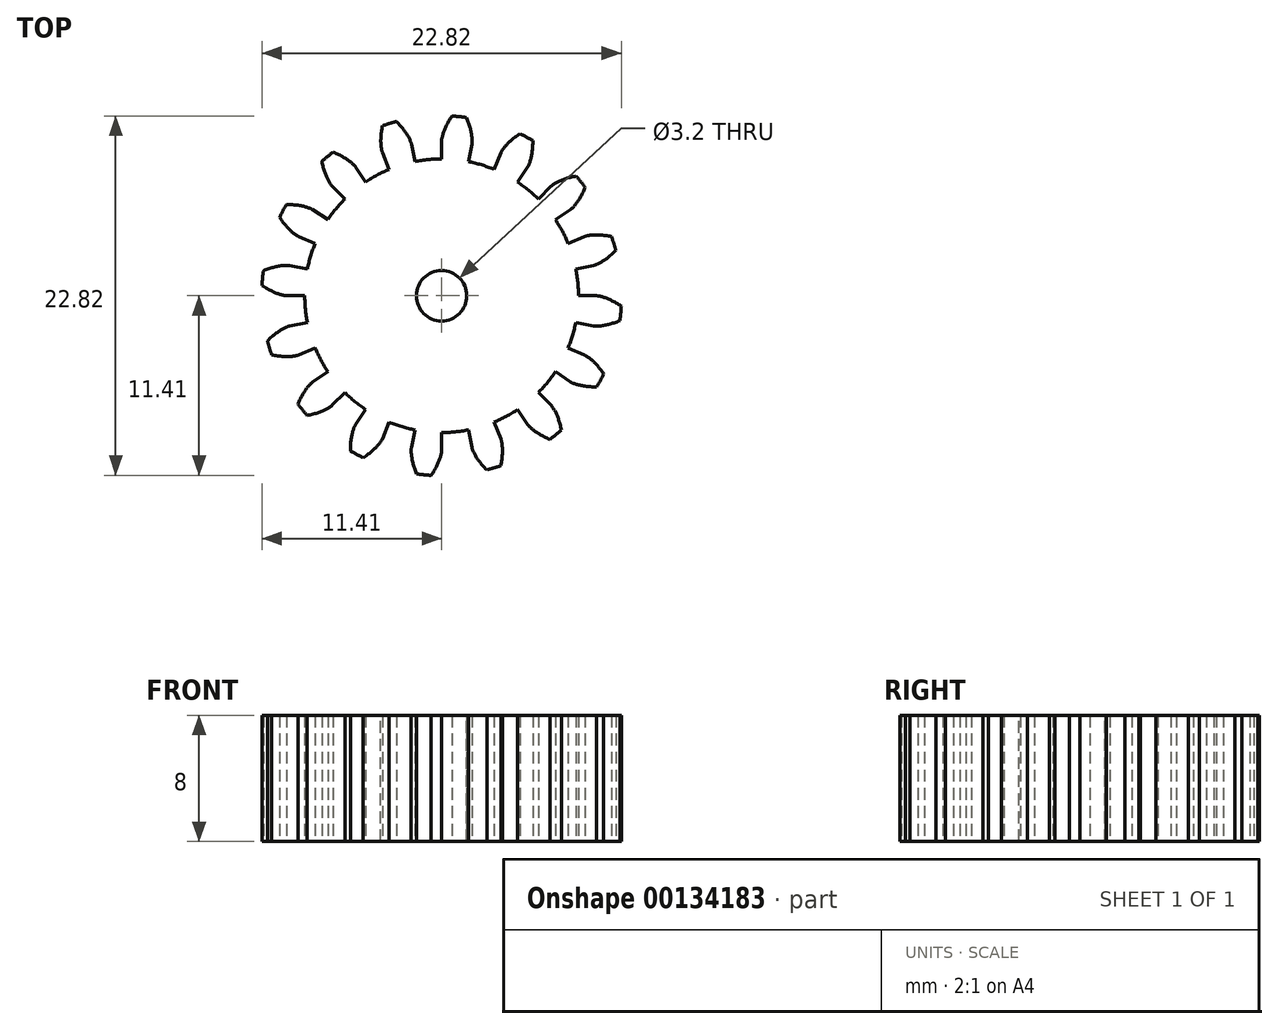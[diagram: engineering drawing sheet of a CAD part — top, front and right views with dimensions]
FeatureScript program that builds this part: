
annotation { "Feature Type Name" : "Feature", "Feature Type Description" : "" }
export const myFeature = defineFeature(function(context is Context, id is Id, definition is map)
    precondition{}
    {
        {
            assignVariable(context, id + "F0", {"name" : "NumberTeeth", "anyValue" : 16});
        }
        {
            assignVariable(context, id + "F1", {"name" : "GearThickness", "anyValue" : 8});
        }
        {
            var Q0;
            Q0=qCreatedBy(makeId("Top.planeOp"),FACE);
            var sketch = newSketch(context, id + "F2", { "sketchPlane" : qUnion([Q0])});
            skCircle(sketch, "E0", {"center": v(0, 0) * mm, "radius": 8.7 * mm});
            skCircle(sketch, "E1", {"center": v(0, 0) * mm, "radius": 9.84 * mm, "construction": true});
            skCircle(sketch, "E2", {"center": v(0, 0) * mm, "radius": 10.16 * mm, "construction": true});
            skCircle(sketch, "E3", {"center": v(0, 0) * mm, "radius": 11.43 * mm});
            skLineSegment(sketch, "E4", {"start": v(0, 0) * mm, "end": v(-9.84, 0) * mm, "construction": true});
            skLineSegment(sketch, "E5.1.0", {"start": v(0, 0) * mm, "end": v(-9.82, 0.5) * mm, "construction": true});
            skLineSegment(sketch, "E5.2.0", {"start": v(0, 0) * mm, "end": v(-9.79, 0.98) * mm, "construction": true});
            skLineSegment(sketch, "E5.3.0", {"start": v(0, 0) * mm, "end": v(-9.73, 1.47) * mm, "construction": true});
            skLineSegment(sketch, "E5.4.0", {"start": v(0, 0) * mm, "end": v(-9.64, 1.95) * mm, "construction": true});
            skLineSegment(sketch, "E5.5.0", {"start": v(0, 0) * mm, "end": v(-9.53, 2.43) * mm, "construction": true});
            skLineSegment(sketch, "E5.6.0", {"start": v(0, 0) * mm, "end": v(-9.4, 2.9) * mm, "construction": true});
            skLineSegment(sketch, "E5.7.0", {"start": v(0, 0) * mm, "end": v(-9.24, 3.37) * mm, "construction": true});
            skLineSegment(sketch, "E5.8.0", {"start": v(0, 0) * mm, "end": v(-9.06, 3.83) * mm, "construction": true});
            skLineSegment(sketch, "E5.9.0", {"start": v(0, 0) * mm, "end": v(-8.86, 4.28) * mm, "construction": true});
            skLineSegment(sketch, "E5.10.0", {"start": v(0, 0) * mm, "end": v(-8.63, 4.72) * mm, "construction": true});
            skLineSegment(sketch, "E5.11.0", {"start": v(0, 0) * mm, "end": v(-8.39, 5.14) * mm, "construction": true});
            skLineSegment(sketch, "E5.12.0", {"start": v(0, 0) * mm, "end": v(-8.12, 5.55) * mm, "construction": true});
            skLineSegment(sketch, "E5.13.0", {"start": v(0, 0) * mm, "end": v(-7.83, 5.95) * mm, "construction": true});
            skLineSegment(sketch, "E5.14.0", {"start": v(0, 0) * mm, "end": v(-7.52, 6.34) * mm, "construction": true});
            skLineSegment(sketch, "E5.anchor2", {"start": v(0, 0) * mm, "end": v(-7.52, 6.34) * mm, "construction": true});
            skLineSegment(sketch, "E6", {"start": v(-9.82, 0.5) * mm, "end": v(-9.85, 0) * mm, "construction": true});
            skLineSegment(sketch, "E7", {"start": v(-9.79, 0.98) * mm, "end": v(-9.89, 0) * mm, "construction": true});
            skLineSegment(sketch, "E8", {"start": v(-9.73, 1.47) * mm, "end": v(-9.95, 0.01) * mm, "construction": true});
            skLineSegment(sketch, "E9", {"start": v(-9.53, 2.43) * mm, "end": v(-10.14, 0.05) * mm, "construction": true});
            skLineSegment(sketch, "E10", {"start": v(-9.4, 2.9) * mm, "end": v(-10.27, 0.09) * mm, "construction": true});
            skLineSegment(sketch, "E11", {"start": v(-9.24, 3.37) * mm, "end": v(-10.42, 0.14) * mm, "construction": true});
            skLineSegment(sketch, "E12", {"start": v(-9.06, 3.83) * mm, "end": v(-10.6, 0.2) * mm, "construction": true});
            skLineSegment(sketch, "E13", {"start": v(-8.86, 4.28) * mm, "end": v(-10.78, 0.3) * mm, "construction": true});
            skLineSegment(sketch, "E14", {"start": v(-8.63, 4.72) * mm, "end": v(-11, 0.4) * mm, "construction": true});
            skLineSegment(sketch, "E15", {"start": v(-8.39, 5.14) * mm, "end": v(-11.21, 0.53) * mm, "construction": true});
            skLineSegment(sketch, "E16", {"start": v(-9.64, 1.95) * mm, "end": v(-10.03, 0.03) * mm, "construction": true});
            skLineSegment(sketch, "E17", {"start": v(-8.12, 5.55) * mm, "end": v(-11.45, 0.68) * mm, "construction": true});
            skLineSegment(sketch, "E18", {"start": v(-7.83, 5.95) * mm, "end": v(-11.7, 0.86) * mm, "construction": true});
            skLineSegment(sketch, "E19", {"start": v(-7.52, 6.34) * mm, "end": v(-11.96, 1.07) * mm, "construction": true});
            skLineSegment(sketch, "E20", {"start": v(0, 0) * mm, "end": v(-9.79, 0.96) * mm, "construction": true});
            skLineSegment(sketch, "E21", {"start": v(-8.7, 0) * mm, "end": v(-9.84, 0) * mm});
            skLineSegment(sketch, "E22.MirrorCS", {"start": v(-8.52, 1.7) * mm, "end": v(-9.65, 1.92) * mm});
            skFitSpline(sketch, "E23", {"points": [v(-9.84, 0) * mm, v(-9.85, 0) * mm, v(-9.89, 0) * mm, v(-9.95, 0.01) * mm, v(-10.03, 0.03) * mm, v(-10.14, 0.05) * mm, v(-10.27, 0.09) * mm, v(-10.42, 0.14) * mm, v(-10.6, 0.2) * mm, v(-10.78, 0.3) * mm, v(-11, 0.4) * mm, v(-11.21, 0.53) * mm, v(-11.45, 0.68) * mm, v(-11.7, 0.86) * mm, v(-11.96, 1.07) * mm], "startDerivative": vector(-0.85, 0) * mm, "endDerivative": vector(-1.05, 0.88) * mm});
            skLineSegment(sketch, "E24", {"start": v(-11.96, 1.07) * mm, "end": v(-16.54, 4.93) * mm, "construction": true});
            skFitSpline(sketch, "E25.MirrorCS", {"points": [v(-9.65, 1.92) * mm, v(-9.66, 1.92) * mm, v(-9.7, 1.93) * mm, v(-9.76, 1.93) * mm, v(-9.84, 1.93) * mm, v(-9.95, 1.93) * mm, v(-10.09, 1.92) * mm, v(-10.25, 1.9) * mm, v(-10.43, 1.86) * mm, v(-10.63, 1.82) * mm, v(-10.86, 1.75) * mm, v(-11.1, 1.67) * mm, v(-11.36, 1.56) * mm, v(-11.64, 1.44) * mm, v(-11.94, 1.28) * mm], "startDerivative": vector(-0.84, 0.17) * mm, "endDerivative": vector(-1.2, -0.66) * mm});
            skSolve(sketch);
        }
        {
            var Q0;
            {var subQ0=sQuery(id+"F2.wireOp",EDGE,"E0");var subQ27=makeQuery(id+"F2.imprint","INTERSECT",VERTEX,{"derivedFrom":[subQ0,sQuery(id+"F2.wireOp",EDGE,"10ea1024-8cf5-41f5-a75f-a634b86921f3.10.0")]});Q0=makeQuery(id+"F2.imprint","IMPRINT",FACE,{"disambiguationData":[TD([[makeQuery(id+"F2.imprint","IMPRINT",EDGE,{"disambiguationData":[TD([[subQ27,-1.0]])],"derivedFrom":subQ0}),1.0]])]});}
            var Q1;
            {var subQ0=sQuery(id+"F2.wireOp",EDGE,"10ea1024-8cf5-41f5-a75f-a634b86921f3.1.0");Q1=makeQuery(id+"F2.imprint","IMPRINT",FACE,{"disambiguationData":[TD([[makeQuery(id+"F2.imprint","IMPRINT",EDGE,{"derivedFrom":subQ0}),-1.0]])]});}
            var Q2;
            {var subQ7=sQuery(id+"F2.wireOp",EDGE,"10ea1024-8cf5-41f5-a75f-a634b86921f3.2.0");Q2=makeQuery(id+"F2.imprint","IMPRINT",FACE,{"disambiguationData":[TD([[makeQuery(id+"F2.imprint","IMPRINT",EDGE,{"derivedFrom":subQ7}),-1.0]])]});}
            var Q3;
            {var subQ8=sQuery(id+"F2.wireOp",EDGE,"10ea1024-8cf5-41f5-a75f-a634b86921f3.3.0");Q3=makeQuery(id+"F2.imprint","IMPRINT",FACE,{"disambiguationData":[TD([[makeQuery(id+"F2.imprint","IMPRINT",EDGE,{"derivedFrom":subQ8}),-1.0]])]});}
            var Q4;
            {var subQ2=sQuery(id+"F2.wireOp",EDGE,"10ea1024-8cf5-41f5-a75f-a634b86921f3.4.0");Q4=makeQuery(id+"F2.imprint","IMPRINT",FACE,{"disambiguationData":[TD([[makeQuery(id+"F2.imprint","IMPRINT",EDGE,{"derivedFrom":subQ2}),-1.0]])]});}
            var Q5;
            {var subQ8=sQuery(id+"F2.wireOp",EDGE,"10ea1024-8cf5-41f5-a75f-a634b86921f3.5.0");Q5=makeQuery(id+"F2.imprint","IMPRINT",FACE,{"disambiguationData":[TD([[makeQuery(id+"F2.imprint","IMPRINT",EDGE,{"derivedFrom":subQ8}),-1.0]])]});}
            var Q6;
            {var subQ3=sQuery(id+"F2.wireOp",EDGE,"10ea1024-8cf5-41f5-a75f-a634b86921f3.6.0");Q6=makeQuery(id+"F2.imprint","IMPRINT",FACE,{"disambiguationData":[TD([[makeQuery(id+"F2.imprint","IMPRINT",EDGE,{"derivedFrom":subQ3}),-1.0]])]});}
            var Q7;
            {var subQ0=sQuery(id+"F2.wireOp",EDGE,"10ea1024-8cf5-41f5-a75f-a634b86921f3.7.0");Q7=makeQuery(id+"F2.imprint","IMPRINT",FACE,{"disambiguationData":[TD([[makeQuery(id+"F2.imprint","IMPRINT",EDGE,{"derivedFrom":subQ0}),-1.0]])]});}
            var Q8;
            {var subQ5=sQuery(id+"F2.wireOp",EDGE,"10ea1024-8cf5-41f5-a75f-a634b86921f3.8.0");Q8=makeQuery(id+"F2.imprint","IMPRINT",FACE,{"disambiguationData":[TD([[makeQuery(id+"F2.imprint","IMPRINT",EDGE,{"derivedFrom":subQ5}),-1.0]])]});}
            var Q9;
            {var subQ1=sQuery(id+"F2.wireOp",EDGE,"10ea1024-8cf5-41f5-a75f-a634b86921f3.9.0");Q9=makeQuery(id+"F2.imprint","IMPRINT",FACE,{"disambiguationData":[TD([[makeQuery(id+"F2.imprint","IMPRINT",EDGE,{"derivedFrom":subQ1}),-1.0]])]});}
            var Q10;
            {var subQ5=sQuery(id+"F2.wireOp",EDGE,"10ea1024-8cf5-41f5-a75f-a634b86921f3.10.0");Q10=makeQuery(id+"F2.imprint","IMPRINT",FACE,{"disambiguationData":[TD([[makeQuery(id+"F2.imprint","IMPRINT",EDGE,{"derivedFrom":subQ5}),-1.0]])]});}
            var Q11;
            {var subQ8=sQuery(id+"F2.wireOp",EDGE,"10ea1024-8cf5-41f5-a75f-a634b86921f3.11.0");Q11=makeQuery(id+"F2.imprint","IMPRINT",FACE,{"disambiguationData":[TD([[makeQuery(id+"F2.imprint","IMPRINT",EDGE,{"derivedFrom":subQ8}),-1.0]])]});}
            var Q12;
            {var subQ2=sQuery(id+"F2.wireOp",EDGE,"10ea1024-8cf5-41f5-a75f-a634b86921f3.12.0");Q12=makeQuery(id+"F2.imprint","IMPRINT",FACE,{"disambiguationData":[TD([[makeQuery(id+"F2.imprint","IMPRINT",EDGE,{"derivedFrom":subQ2}),-1.0]])]});}
            var Q13;
            {var subQ3=sQuery(id+"F2.wireOp",EDGE,"10ea1024-8cf5-41f5-a75f-a634b86921f3.13.0");Q13=makeQuery(id+"F2.imprint","IMPRINT",FACE,{"disambiguationData":[TD([[makeQuery(id+"F2.imprint","IMPRINT",EDGE,{"derivedFrom":subQ3}),-1.0]])]});}
            var Q14;
            {var subQ0=sQuery(id+"F2.wireOp",EDGE,"10ea1024-8cf5-41f5-a75f-a634b86921f3.14.0");Q14=makeQuery(id+"F2.imprint","IMPRINT",FACE,{"disambiguationData":[TD([[makeQuery(id+"F2.imprint","IMPRINT",EDGE,{"derivedFrom":subQ0}),-1.0]])]});}
            var Q15;
            {var subQ6=sQuery(id+"F2.wireOp",EDGE,"10ea1024-8cf5-41f5-a75f-a634b86921f3.15.0");Q15=makeQuery(id+"F2.imprint","IMPRINT",FACE,{"disambiguationData":[TD([[makeQuery(id+"F2.imprint","IMPRINT",EDGE,{"derivedFrom":subQ6}),-1.0]])]});}
            var Q16;
            {var subQ5=sQuery(id+"F2.wireOp",EDGE,"10ea1024-8cf5-41f5-a75f-a634b86921f3.16.0");Q16=makeQuery(id+"F2.imprint","IMPRINT",FACE,{"disambiguationData":[TD([[makeQuery(id+"F2.imprint","IMPRINT",EDGE,{"derivedFrom":subQ5}),-1.0]])]});}
            var Q17;
            {var subQ7=sQuery(id+"F2.wireOp",EDGE,"10ea1024-8cf5-41f5-a75f-a634b86921f3.17.0");Q17=makeQuery(id+"F2.imprint","IMPRINT",FACE,{"disambiguationData":[TD([[makeQuery(id+"F2.imprint","IMPRINT",EDGE,{"derivedFrom":subQ7}),-1.0]])]});}
            var Q18;
            {var subQ5=sQuery(id+"F2.wireOp",EDGE,"10ea1024-8cf5-41f5-a75f-a634b86921f3.18.0");Q18=makeQuery(id+"F2.imprint","IMPRINT",FACE,{"disambiguationData":[TD([[makeQuery(id+"F2.imprint","IMPRINT",EDGE,{"derivedFrom":subQ5}),-1.0]])]});}
            var Q19;
            {var subQ8=sQuery(id+"F2.wireOp",EDGE,"10ea1024-8cf5-41f5-a75f-a634b86921f3.19.0");Q19=makeQuery(id+"F2.imprint","IMPRINT",FACE,{"disambiguationData":[TD([[makeQuery(id+"F2.imprint","IMPRINT",EDGE,{"derivedFrom":subQ8}),-1.0]])]});}
            var Q20;
            {var subQ8=sQuery(id+"F2.wireOp",EDGE,"E21");Q20=makeQuery(id+"F2.imprint","IMPRINT",FACE,{"disambiguationData":[TD([[makeQuery(id+"F2.imprint","IMPRINT",EDGE,{"derivedFrom":subQ8}),-1.0]])]});}
            extrude(context, id + "F3", {"entities" : qUnion([Q0, Q1, Q2, Q3, Q4, Q5, Q6, Q7, Q8, Q9, Q10, Q11, Q12, Q13, Q14, Q15, Q16, Q17, Q18, Q19, Q20]), "depth" : (getVariable(context, 'GearThickness')) * mm});
        }
        {
            var Q0;
            Q0=makeQuery(id+"F3.opExtrude","SWEPT_FACE",FACE,{"disambiguationData":[OSD([sQuery(id+"F2.wireOp",EDGE,"E25.MirrorCS")])]});
            var Q1;
            Q1=makeQuery(id+"F3.opExtrude","SWEPT_FACE",FACE,{"disambiguationData":[OSD([sQuery(id+"F2.wireOp",EDGE,"E23")])]});
            var Q2;
            Q2=makeQuery(id+"F3.opExtrude","SWEPT_FACE",FACE,{"disambiguationData":[OSD([sQuery(id+"F2.wireOp",EDGE,"E3")])]});
            var Q3;
            Q3=makeQuery(id+"F3.opExtrude","SWEPT_FACE",FACE,{"disambiguationData":[OSD([sQuery(id+"F2.wireOp",EDGE,"E22.MirrorCS")])]});
            var Q4;
            Q4=makeQuery(id+"F3.opExtrude","SWEPT_FACE",FACE,{"disambiguationData":[OSD([sQuery(id+"F2.wireOp",EDGE,"E21")])]});
            var Q5;
            Q5=makeQuery(id+"F3.opExtrude","SWEPT_FACE",FACE,{"disambiguationData":[OSD([sQuery(id+"F2.wireOp",EDGE,"E0")])]});
            circularPattern(context, id + "F4", {"faces" : qUnion([Q0, Q1, Q2, Q3, Q4]), "axis" : qUnion([Q5]), "angle" : 360 * degree, "instanceCount" : getVariable(context, 'NumberTeeth'), "equalSpace" : true, "patternType" : PatternType.FACE});
        }
        {
            var Q0;
            Q0=makeQuery(id+"F3.opExtrude","CAP_FACE",FACE,{"disambiguationData":[OSD([sQuery(id+"F2.wireOp",EDGE,"E0"),sQuery(id+"F2.wireOp",EDGE,"E3"),sQuery(id+"F2.wireOp",EDGE,"E21"),sQuery(id+"F2.wireOp",EDGE,"E22.MirrorCS"),sQuery(id+"F2.wireOp",EDGE,"E23"),sQuery(id+"F2.wireOp",EDGE,"E25.MirrorCS")])],"isStart":false});
            var sketch = newSketch(context, id + "F5", { "sketchPlane" : qUnion([Q0])});
            skCircle(sketch, "E26", {"center": v(0, 0) * mm, "radius": 1.6 * mm});
            skSolve(sketch);
        }
        {
            var Q0;
            Q0 = qSketchRegion(id + "F5", true);
            extrude(context, id + "F6", {"entities" : qUnion([Q0]), "operationType" : NewBodyOperationType.REMOVE, "oppositeDirection" : true, "depth" : 25 * mm});
        }
    });
